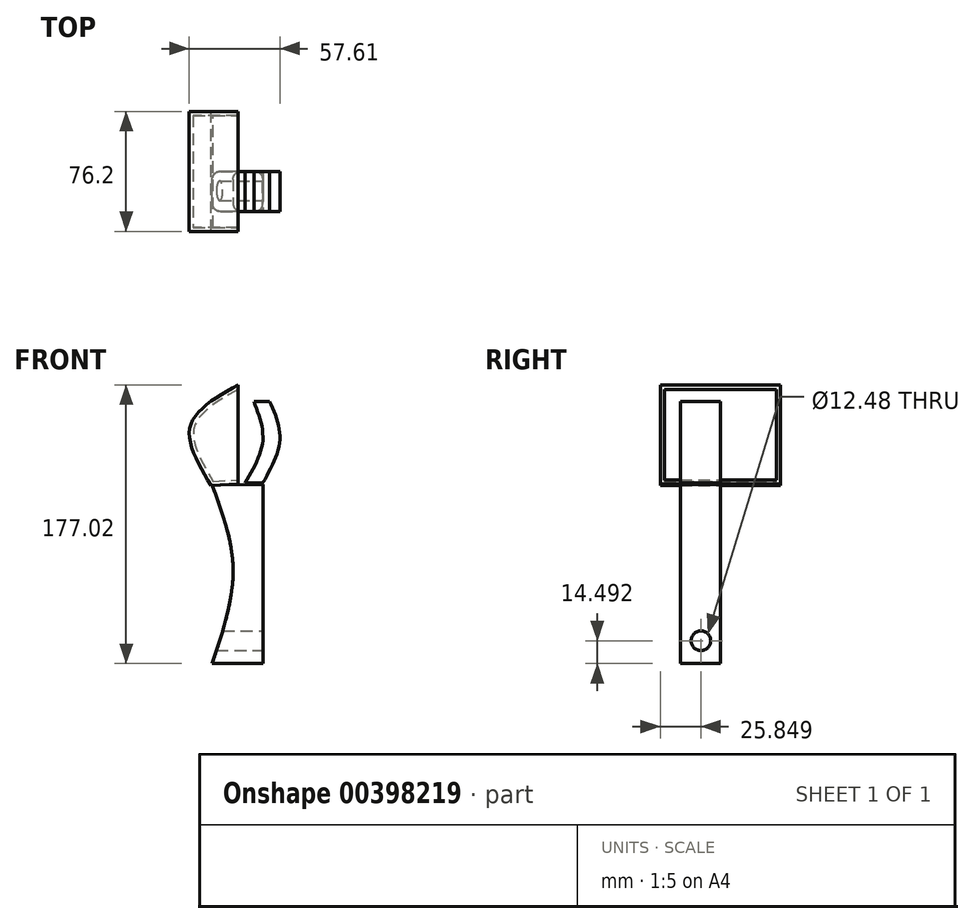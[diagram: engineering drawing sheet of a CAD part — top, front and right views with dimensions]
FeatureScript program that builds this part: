
annotation { "Feature Type Name" : "Feature", "Feature Type Description" : "" }
export const myFeature = defineFeature(function(context is Context, id is Id, definition is map)
    precondition{}
    {
        {
            var Q0;
            Q0=qCreatedBy(makeId("Front.planeOp"),FACE);
            var sketch = newSketch(context, id + "F0", { "sketchPlane" : qUnion([Q0])});
            skLineSegment(sketch, "E0", {"start": v(25.78, 54.34) * mm, "end": v(25.78, -59.5) * mm});
            skLineSegment(sketch, "E1", {"start": v(25.78, -59.5) * mm, "end": v(-6.44, -59.5) * mm});
            skFitSpline(sketch, "E2", {"points": [v(-6.44, -59.5) * mm, v(6.87, 0) * mm, v(-6.44, 53.91) * mm], "startDerivative": vector(39.66, 117.79) * mm, "endDerivative": vector(-40.29, 108.97) * mm});
            skLineSegment(sketch, "E3", {"start": v(-6.44, 53.91) * mm, "end": v(25.78, 54.34) * mm});
            skSolve(sketch);
        }
        {
            var Q0;
            Q0=makeQuery(id+"F0.imprint","IMPRINT",FACE,{"disambiguationData":[TD([[makeQuery(id+"F0.imprint","IMPRINT",EDGE,{"derivedFrom":sQuery(id+"F0.wireOp",EDGE,"E0")}),-1.0]])]});
            extrude(context, id + "F1", {"entities" : qUnion([Q0]), "depth" : 25.4 * mm});
        }
        {
            var Q0;
            Q0=qCreatedBy(makeId("Front.planeOp"),FACE);
            var sketch = newSketch(context, id + "F2", { "sketchPlane" : qUnion([Q0])});
            skLineSegment(sketch, "E4", {"start": v(9.96, 54.57) * mm, "end": v(9.96, 117.52) * mm});
            skFitSpline(sketch, "E5", {"points": [v(9.96, 117.52) * mm, v(-20.38, 91.26) * mm, v(-7.25, 53.67) * mm], "startDerivative": vector(-82.33, -46.7) * mm, "endDerivative": vector(48, -81.04) * mm});
            skLineSegment(sketch, "E6", {"start": v(-7.25, 53.67) * mm, "end": v(9.96, 54.57) * mm});
            skSolve(sketch);
        }
        {
            var Q0;
            Q0=makeQuery(id+"F2.imprint","IMPRINT",FACE,{"disambiguationData":[TD([[makeQuery(id+"F2.imprint","IMPRINT",EDGE,{"derivedFrom":sQuery(id+"F2.wireOp",EDGE,"E4")}),1.0]])]});
            extrude(context, id + "F3", {"entities" : qUnion([Q0]), "endBound" : BoundingType.SYMMETRIC, "depth" : 76.2 * mm});
        }
        {
            var Q0;
            Q0=qCreatedBy(makeId("Front.planeOp"),FACE);
            var sketch = newSketch(context, id + "F4", { "sketchPlane" : qUnion([Q0])});
            skLineSegment(sketch, "E7", {"start": v(14.35, 55.16) * mm, "end": v(25.73, 55.16) * mm});
            skPoint(sketch, "E8.2.internal.snap0", {"position": v(20.04, 55.16) * mm});
            skFitSpline(sketch, "E8", {"points": [v(14.35, 55.16) * mm, v(25.73, 81.88) * mm, v(20.04, 107.1) * mm], "startDerivative": vector(30.82, 51.92) * mm, "endDerivative": vector(-19.93, 51.97) * mm});
            skLineSegment(sketch, "E9", {"start": v(20.04, 107.1) * mm, "end": v(30.18, 107.1) * mm});
            skFitSpline(sketch, "E10", {"points": [v(30.18, 107.1) * mm, v(36.6, 82.87) * mm, v(25.73, 55.16) * mm], "startDerivative": vector(21.65, -50.06) * mm, "endDerivative": vector(-29.82, -53.78) * mm});
            skSolve(sketch);
        }
        {
            var Q0;
            Q0=makeQuery(id+"F4.imprint","IMPRINT",FACE,{"disambiguationData":[TD([[makeQuery(id+"F4.imprint","IMPRINT",EDGE,{"derivedFrom":sQuery(id+"F4.wireOp",EDGE,"E7")}),1.0]])]});
            extrude(context, id + "F5", {"entities" : qUnion([Q0]), "depth" : 25.4 * mm});
        }
        {
            var Q0;
            Q0=makeQuery(id+"F3.opExtrude","SWEPT_FACE",FACE,{"disambiguationData":[OSD([sQuery(id+"F2.wireOp",EDGE,"E4")])]});
            shell(context, id + "F6", {"entities" : qUnion([Q0]), "thickness" : 2.54 * mm});
        }
        {
            var Q0;
            Q0=makeQuery(id+"F1.opExtrude","SWEPT_FACE",FACE,{"disambiguationData":[OSD([sQuery(id+"F0.wireOp",EDGE,"E0")])]});
            var sketch = newSketch(context, id + "F7", { "sketchPlane" : qUnion([Q0])});
            skCircle(sketch, "E11", {"center": v(-12.25, -45) * mm, "radius": 6.24 * mm});
            skSolve(sketch);
        }
        {
            var Q0;
            Q0=makeQuery(id+"F7.imprint","IMPRINT",FACE,{"disambiguationData":[TD([[makeQuery(id+"F7.imprint","IMPRINT",EDGE,{"derivedFrom":sQuery(id+"F7.wireOp",EDGE,"E11")}),1.0]])]});
            extrude(context, id + "F8", {"entities" : qUnion([Q0]), "operationType" : NewBodyOperationType.REMOVE, "oppositeDirection" : true, "depth" : 76.96 * mm});
        }
        {
            var Q0;
            Q0=makeQuery(id+"F1.opExtrude","CAP_EDGE",EDGE,{"disambiguationData":[OSD([sQuery(id+"F0.wireOp",EDGE,"E0")])],"isStart":false});
            var Q1;
            Q1=makeQuery(id+"F1.opExtrude","CAP_EDGE",EDGE,{"disambiguationData":[OSD([sQuery(id+"F0.wireOp",EDGE,"E0")])],"isStart":true});
            var Q2;
            Q2=makeQuery(id+"F1.opExtrude","CAP_EDGE",EDGE,{"disambiguationData":[OSD([sQuery(id+"F0.wireOp",EDGE,"E2")])],"isStart":false});
            var Q3;
            Q3=makeQuery(id+"F1.opExtrude","CAP_EDGE",EDGE,{"disambiguationData":[OSD([sQuery(id+"F0.wireOp",EDGE,"E2")])],"isStart":true});
            fillet(context, id + "F9", {"entities" : qUnion([Q0, Q1, Q2, Q3]), "radius" : 5.08 * mm, "tangentPropagation" : true, "allowEdgeOverflow" : false});
        }
    });
